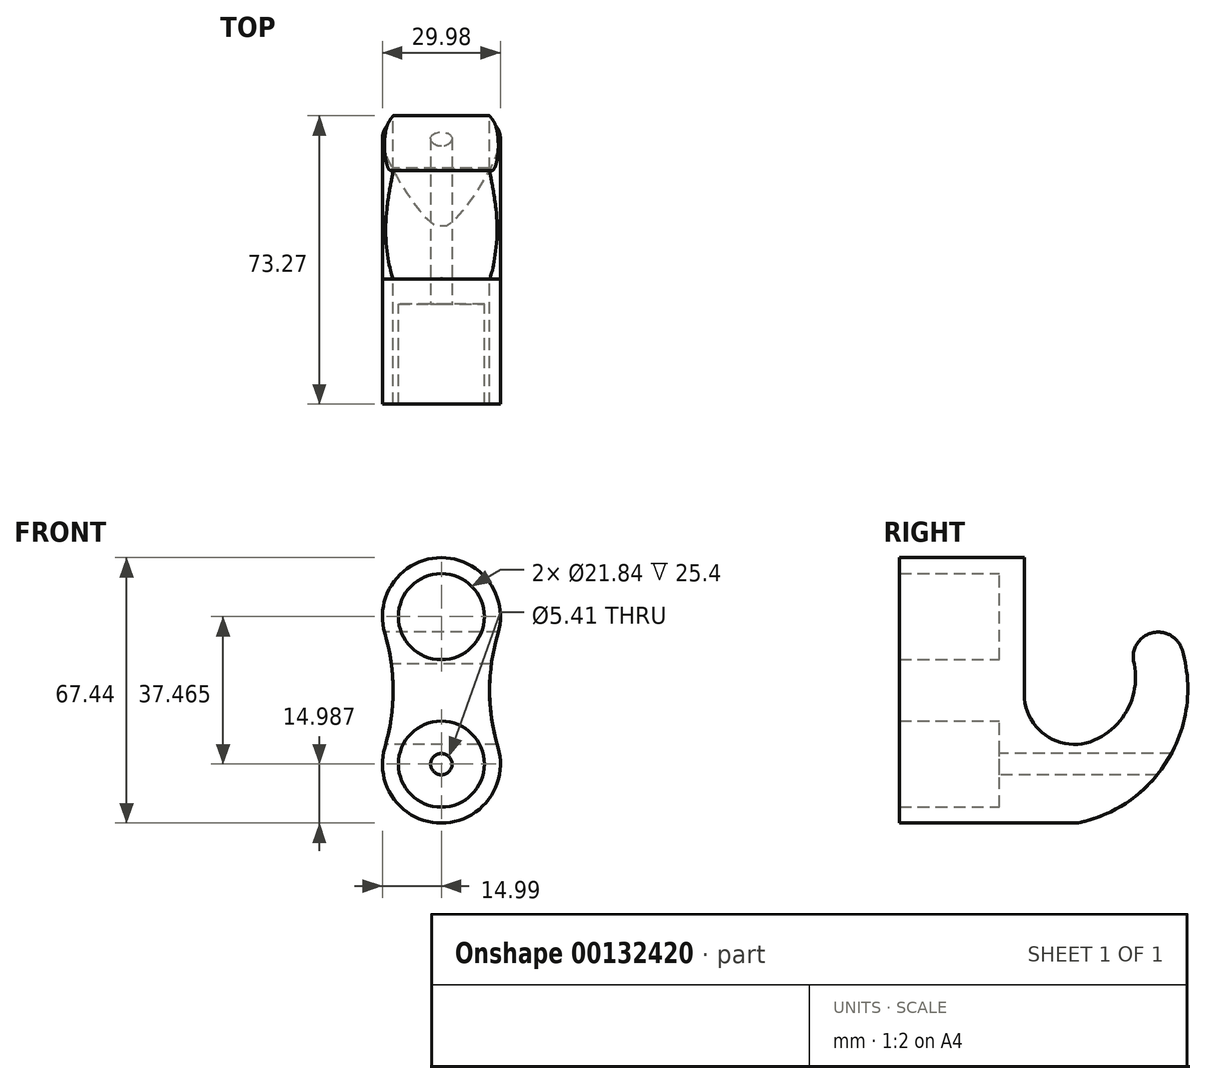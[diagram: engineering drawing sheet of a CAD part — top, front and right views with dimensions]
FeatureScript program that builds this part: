
annotation { "Feature Type Name" : "Feature", "Feature Type Description" : "" }
export const myFeature = defineFeature(function(context is Context, id is Id, definition is map)
    precondition{}
    {
        {
            var Q0;
            Q0=qCreatedBy(makeId("Front.planeOp"),FACE);
            var sketch = newSketch(context, id + "F0", { "sketchPlane" : qUnion([Q0])});
            skCircle(sketch, "E0", {"center": v(0, 18.73) * mm, "radius": 10.92 * mm});
            skCircle(sketch, "E1", {"center": v(0, -18.73) * mm, "radius": 10.92 * mm});
            skLineSegment(sketch, "E2", {"start": v(0, 18.73) * mm, "end": v(0, -18.73) * mm, "construction": true});
            skCircle(sketch, "E3", {"center": v(0, 18.73) * mm, "radius": 14.99 * mm});
            skCircle(sketch, "E4", {"center": v(0, -18.73) * mm, "radius": 14.99 * mm});
            skArc(sketch, "E5", {"start": v(-14.37, -14.47) * mm, "mid": v(-12.26, 0) * mm, "end": v(-14.37, 14.47) * mm});
            skArc(sketch, "E6", {"start": v(14.37, 14.47) * mm, "mid": v(12.26, 0) * mm, "end": v(14.37, -14.47) * mm});
            skSolve(sketch);
        }
        {
            var Q0;
            {var subQ0=sQuery(id+"F0.wireOp",EDGE,"E5");Q0=makeQuery(id+"F0.imprint","IMPRINT",FACE,{"disambiguationData":[TD([[makeQuery(id+"F0.imprint","IMPRINT",EDGE,{"derivedFrom":subQ0}),-1.0]])]});}
            var Q1;
            Q1=makeQuery(id+"F0.imprint","IMPRINT",FACE,{"disambiguationData":[TD([[makeQuery(id+"F0.imprint","IMPRINT",EDGE,{"derivedFrom":sQuery(id+"F0.wireOp",EDGE,"E0")}),-1.0]])]});
            var Q2;
            Q2=makeQuery(id+"F0.imprint","IMPRINT",FACE,{"disambiguationData":[TD([[makeQuery(id+"F0.imprint","IMPRINT",EDGE,{"derivedFrom":sQuery(id+"F0.wireOp",EDGE,"E1")}),-1.0]])]});
            extrude(context, id + "F1", {"entities" : qUnion([Q0, Q1, Q2]), "depth" : 25.4 * mm, "offsetDistance" : 25.4 * mm});
        }
        {
            var Q0;
            Q0 = qSketchRegion(id + "F0", true);
            var Q1;
            Q1=makeQuery(id+"F0.imprint","IMPRINT",FACE,{"disambiguationData":[TD([[makeQuery(id+"F0.imprint","IMPRINT",EDGE,{"derivedFrom":sQuery(id+"F0.wireOp",EDGE,"E0")}),1.0]])]});
            var Q2;
            Q2=makeQuery(id+"F0.imprint","IMPRINT",FACE,{"disambiguationData":[TD([[makeQuery(id+"F0.imprint","IMPRINT",EDGE,{"derivedFrom":sQuery(id+"F0.wireOp",EDGE,"E1")}),1.0]])]});
            extrude(context, id + "F2", {"entities" : qUnion([Q0, Q1, Q2]), "operationType" : NewBodyOperationType.ADD, "oppositeDirection" : true, "depth" : 6.35 * mm});
        }
        {
            var Q0;
            Q0=qCreatedBy(makeId("Right.planeOp"),FACE);
            var sketch = newSketch(context, id + "F3", { "sketchPlane" : qUnion([Q0])});
            skArc(sketch, "E7", {"start": v(6.35, -33.67) * mm, "mid": v(38.78, -23) * mm, "end": v(46.44, 10.26) * mm});
            skArc(sketch, "E8", {"start": v(0, 0) * mm, "mid": v(20.46, -13.8) * mm, "end": v(34.26, 6.66) * mm});
            skArc(sketch, "E9", {"start": v(46.44, 10.26) * mm, "mid": v(38.56, 14.55) * mm, "end": v(34.26, 6.66) * mm});
            skPoint(sketch, "E10", {"position": v(0, 0) * mm});
            skLineSegment(sketch, "E11", {"start": v(0, 0) * mm, "end": v(6.35, -33.67) * mm});
            skSolve(sketch);
        }
        {
            var Q0;
            Q0=makeQuery(id+"F3.imprint","IMPRINT",FACE,{"disambiguationData":[TD([[makeQuery(id+"F3.imprint","IMPRINT",EDGE,{"derivedFrom":sQuery(id+"F3.wireOp",EDGE,"E7")}),1.0]])]});
            extrude(context, id + "F4", {"entities" : qUnion([Q0]), "operationType" : NewBodyOperationType.ADD, "endBound" : BoundingType.SYMMETRIC, "depth" : 50.8 * mm});
        }
        {
            var Q0;
            Q0 = qSketchRegion(id + "F0", true);
            var Q1;
            Q1=makeQuery(id+"F0.imprint","IMPRINT",FACE,{"disambiguationData":[TD([[makeQuery(id+"F0.imprint","IMPRINT",EDGE,{"derivedFrom":sQuery(id+"F0.wireOp",EDGE,"E1")}),1.0]])]});
            var Q2;
            Q2=makeQuery(id+"F0.imprint","IMPRINT",FACE,{"disambiguationData":[TD([[makeQuery(id+"F0.imprint","IMPRINT",EDGE,{"derivedFrom":sQuery(id+"F0.wireOp",EDGE,"E0")}),1.0]])]});
            extrude(context, id + "F5", {"entities" : qUnion([Q0, Q1, Q2]), "operationType" : NewBodyOperationType.INTERSECT, "oppositeDirection" : true, "depth" : 76.2 * mm});
        }
        {
            var Q0;
            Q0=makeQuery(id+"F0.imprint","IMPRINT",FACE,{"disambiguationData":[TD([[makeQuery(id+"F0.imprint","IMPRINT",EDGE,{"derivedFrom":sQuery(id+"F0.wireOp",EDGE,"E0")}),-1.0]])]});
            var Q1;
            {var subQ0=sQuery(id+"F0.wireOp",EDGE,"E5");Q1=makeQuery(id+"F0.imprint","IMPRINT",FACE,{"disambiguationData":[TD([[makeQuery(id+"F0.imprint","IMPRINT",EDGE,{"derivedFrom":subQ0}),-1.0]])]});}
            var Q2;
            Q2=makeQuery(id+"F0.imprint","IMPRINT",FACE,{"disambiguationData":[TD([[makeQuery(id+"F0.imprint","IMPRINT",EDGE,{"derivedFrom":sQuery(id+"F0.wireOp",EDGE,"E1")}),-1.0]])]});
            var Q3;
            Q3=sQuery(id+"F0.wireOp",EDGE,"E3");
            extrude(context, id + "F6", {"entities" : qUnion([Q0, Q1, Q2]), "operationType" : NewBodyOperationType.ADD, "surfaceEntities" : qUnion([Q3]), "depth" : 25.4 * mm});
        }
        {
            var Q0;
            Q0=sQuery(id+"F0.wireOp",VERTEX,"E4.center");
            var Q1;
            Q1=makeQuery(id+"F1.opExtrude","SWEPT_BODY",BODY,{"disambiguationData":[OSD([sQuery(id+"F0.wireOp",EDGE,"E0"),sQuery(id+"F0.wireOp",EDGE,"E1"),sQuery(id+"F0.wireOp",EDGE,"E3"),sQuery(id+"F0.wireOp",EDGE,"E4"),sQuery(id+"F0.wireOp",EDGE,"E5"),sQuery(id+"F0.wireOp",EDGE,"E6")])]});
            hole(context, id + "F7", {"style" : HoleStyle.SIMPLE, "endStyle" : HoleEndStyle.THROUGH, "standardTappedOrClearance" : lookupTablePath({ "standard" : "ANSI", "engagement" : "75%", "pitch" : "28 tpi", "size" : "1/4", "type" : "Tapped" }), "standardBlindInLast" : lookupTablePath({ "standard" : "ANSI", "engagement" : "75%", "pitch" : "28 tpi", "size" : "1/4", "type" : "Tapped" }), "holeDiameter" : 5.4 * mm, "locations" : qUnion([Q0]), "scope" : qUnion([Q1]), "isTappedThrough" : true, "majorDiameter" : 6.35 * mm, "showTappedDepth" : true});
        }
        {
            var Q0;
            Q0=makeQuery(id+"F4.boolean.opBoolean","INTERSECT",EDGE,{"derivedFrom":[makeQuery(id+"F2.opExtrude","CAP_FACE",FACE,{"disambiguationData":[OSD([sQuery(id+"F0.wireOp",EDGE,"E3"),sQuery(id+"F0.wireOp",EDGE,"E4"),sQuery(id+"F0.wireOp",EDGE,"E5"),sQuery(id+"F0.wireOp",EDGE,"E6")])],"isStart":false}),makeQuery(id+"F4.opExtrude","SWEPT_FACE",FACE,{"disambiguationData":[OSD([sQuery(id+"F3.wireOp",EDGE,"E8")])]})]});
            fillet(context, id + "F8", {"entities" : qUnion([Q0]), "radius" : 12.7 * mm, "tangentPropagation" : true, "allowEdgeOverflow" : false});
        }
    });
